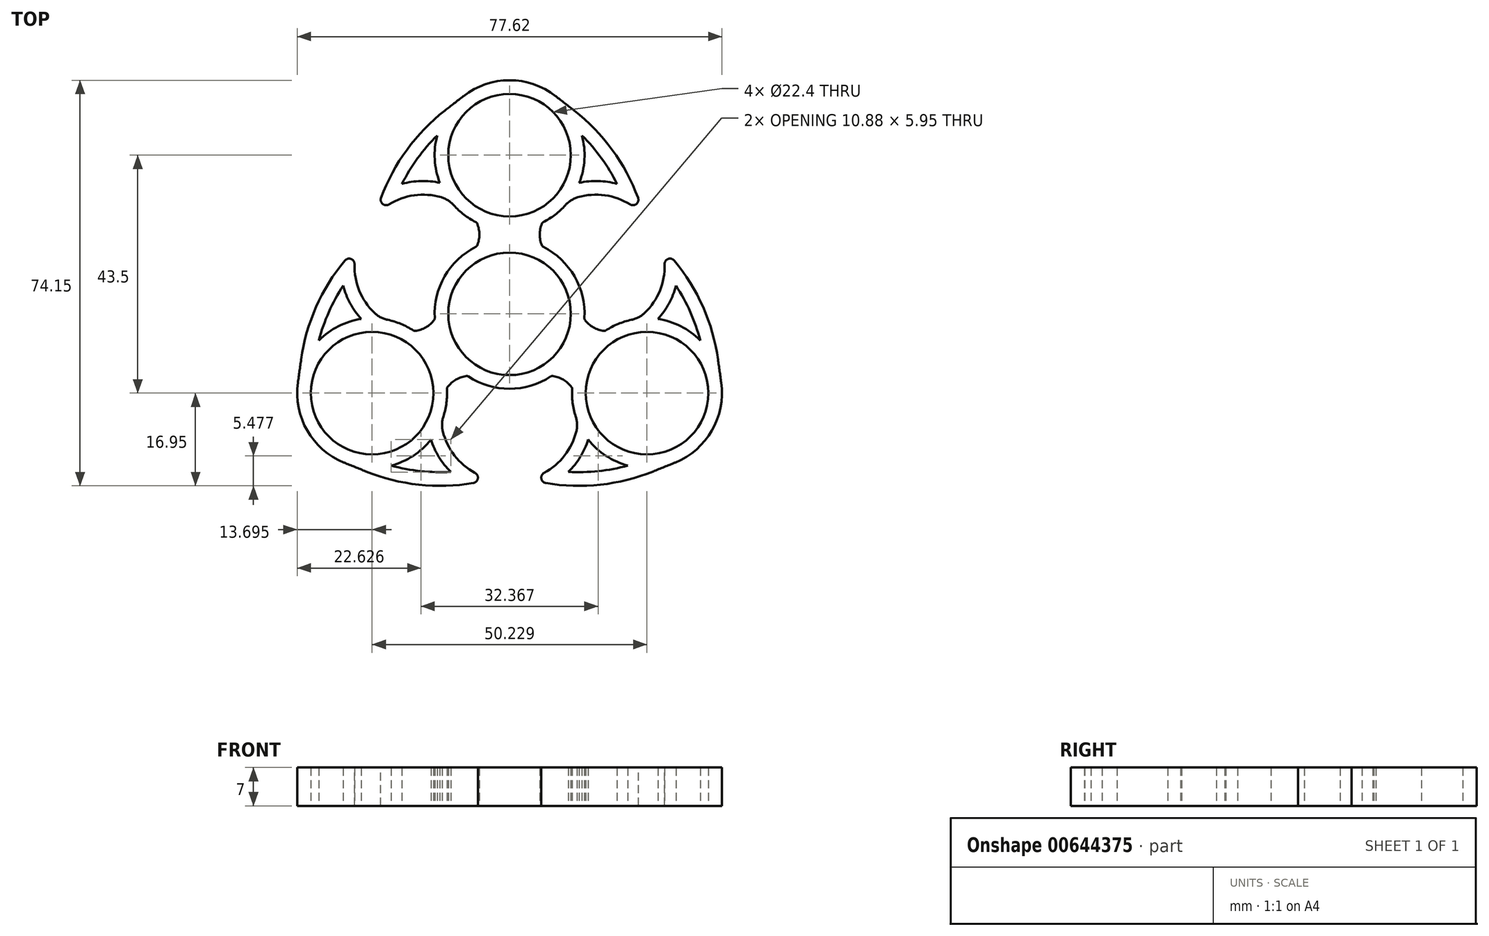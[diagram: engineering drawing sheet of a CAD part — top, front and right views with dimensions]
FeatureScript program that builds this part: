
annotation { "Feature Type Name" : "Feature", "Feature Type Description" : "" }
export const myFeature = defineFeature(function(context is Context, id is Id, definition is map)
    precondition{}
    {
        {
            var Q0;
            Q0=qCreatedBy(makeId("Top.planeOp"),FACE);
            var sketch = newSketch(context, id + "F0", { "sketchPlane" : qUnion([Q0])});
            skCircle(sketch, "E0", {"center": v(0, 0) * mm, "radius": 11.2 * mm});
            skLineSegment(sketch, "E1", {"start": v(0, 0) * mm, "end": v(0, 29) * mm, "construction": true});
            skCircle(sketch, "E2", {"center": v(0, 29) * mm, "radius": 11.2 * mm});
            skLineSegment(sketch, "E3", {"start": v(-11.2, 0) * mm, "end": v(11.2, 0) * mm, "construction": true});
            skLineSegment(sketch, "E4", {"start": v(-11.2, 29) * mm, "end": v(11.2, 29) * mm, "construction": true});
            skArc(sketch, "E5.0", {"start": v(-6, 12.32) * mm, "mid": v(0, -13.7) * mm, "end": v(6, 12.32) * mm});
            skLineSegment(sketch, "E6", {"start": v(0, 42.7) * mm, "end": v(0, 15.3) * mm, "construction": true});
            skLineSegment(sketch, "E7.0", {"start": v(6, 9.46) * mm, "end": v(6, 19.54) * mm, "construction": true});
            skArc(sketch, "E8", {"start": v(6, 16.68) * mm, "mid": v(5.52, 14.5) * mm, "end": v(6, 12.32) * mm});
            skArc(sketch, "E9.MirrorCS", {"start": v(-6, 16.68) * mm, "mid": v(-5.52, 14.5) * mm, "end": v(-6, 12.32) * mm});
            skArc(sketch, "E10.trimOffspring", {"start": v(6, 16.68) * mm, "mid": v(8.7, 18.4) * mm, "end": v(10.9, 20.71) * mm});
            skArc(sketch, "E11", {"start": v(24.52, 17.91) * mm, "mid": v(19, 29.66) * mm, "end": v(9.67, 38.7) * mm});
            skArc(sketch, "E12", {"start": v(24.52, 17.91) * mm, "mid": v(18.17, 21.54) * mm, "end": v(10.9, 20.71) * mm});
            skArc(sketch, "E13.0", {"start": v(19.65, 23.75) * mm, "mid": v(16.2, 24.27) * mm, "end": v(12.73, 23.95) * mm});
            skArc(sketch, "E13.1", {"start": v(19.65, 23.75) * mm, "mid": v(16.8, 28.44) * mm, "end": v(13.22, 32.6) * mm});
            skArc(sketch, "E14.trimOffspring", {"start": v(9.67, 38.7) * mm, "mid": v(-11.16, 36.94) * mm, "end": v(-6, 16.68) * mm});
            skArc(sketch, "E15.trimOffspring", {"start": v(12.73, 23.95) * mm, "mid": v(13.68, 28.23) * mm, "end": v(13.22, 32.6) * mm});
            skSolve(sketch);
        }
        {
            var Q0;
            Q0 = qSketchRegion(id + "F0", true);
            extrude(context, id + "F1", {"entities" : qUnion([Q0]), "depth" : 7 * mm, "offsetDistance" : 25 * mm});
        }
        {
            var Q0;
            Q0=qCreatedBy(makeId("Right.planeOp"),FACE);
            var sketch = newSketch(context, id + "F2", { "sketchPlane" : qUnion([Q0])});
            skLineSegment(sketch, "E16", {"start": v(0, 0) * mm, "end": v(0, 24.15) * mm, "construction": true});
            skSolve(sketch);
        }
        {
            var Q0;
            Q0=makeQuery(id+"F1.opExtrude","SWEPT_EDGE",EDGE,{"disambiguationData":[OSD([sQuery(id+"F0.wireOp",EDGE,"E11"),sQuery(id+"F0.wireOp",EDGE,"E12")])]});
            fillet(context, id + "F3", {"entities" : qUnion([Q0]), "radius" : 1 * mm, "tangentPropagation" : true, "allowEdgeOverflow" : false});
        }
        {
            var Q0;
            Q0=makeQuery(id+"F1.opExtrude","SWEPT_EDGE",EDGE,{"disambiguationData":[OSD([sQuery(id+"F0.wireOp",EDGE,"E10.trimOffspring"),sQuery(id+"F0.wireOp",EDGE,"E12")])]});
            fillet(context, id + "F4", {"entities" : qUnion([Q0]), "radius" : 5 * mm, "tangentPropagation" : true, "allowEdgeOverflow" : false});
        }
        {
            var Q0;
            Q0=makeQuery(id+"F1.opExtrude","SWEPT_EDGE",EDGE,{"disambiguationData":[OSD([sQuery(id+"F0.wireOp",EDGE,"E8"),sQuery(id+"F0.wireOp",EDGE,"a7715e3d-49e1-4b64-8228-6264ce36ffdd.trimOffspring")])]});
            var Q1;
            Q1=makeQuery(id+"F1.opExtrude","SWEPT_EDGE",EDGE,{"disambiguationData":[OSD([sQuery(id+"F0.wireOp",EDGE,"vL0yK9kr-aUAw-fq5m-LhdP-4na97wzfjfiJ"),sQuery(id+"F0.wireOp",EDGE,"a7715e3d-49e1-4b64-8228-6264ce36ffdd.trimOffspring")])]});
            var Q2;
            Q2=makeQuery(id+"F1.opExtrude","SWEPT_EDGE",EDGE,{"disambiguationData":[OSD([sQuery(id+"F0.wireOp",EDGE,"0uLAjghk-3gFu-Hscj-w9fE-ttjJYeJmuMDI"),sQuery(id+"F0.wireOp",EDGE,"vL0yK9kr-aUAw-fq5m-LhdP-4na97wzfjfiJ")])]});
            var Q3;
            Q3=makeQuery(id+"F1.opExtrude","SWEPT_EDGE",EDGE,{"disambiguationData":[OSD([sQuery(id+"F0.wireOp",EDGE,"59cc2289-ca77-47a6-96da-44b8b7f5bab30.MirrorCS"),sQuery(id+"F0.wireOp",EDGE,"5cff57ee-30ec-4a3f-ae05-e4d68d5af566.0")])]});
            var Q4;
            Q4=makeQuery(id+"F1.opExtrude","SWEPT_EDGE",EDGE,{"disambiguationData":[OSD([sQuery(id+"F0.wireOp",EDGE,"Nf5N08YX-LUpC-YIFK-iieG-ll9huf0In2a7"),sQuery(id+"F0.wireOp",EDGE,"59cc2289-ca77-47a6-96da-44b8b7f5bab30.MirrorCS")])]});
            var Q5;
            Q5=makeQuery(id+"F1.opExtrude","SWEPT_EDGE",EDGE,{"disambiguationData":[OSD([sQuery(id+"F0.wireOp",EDGE,"Nf5N08YX-LUpC-YIFK-iieG-ll9huf0In2a7"),sQuery(id+"F0.wireOp",EDGE,"8e5a45cd-34c5-40eb-b1f5-600c90d6d9e0.0")])]});
            var Q6;
            Q6=makeQuery(id+"F1.opExtrude","SWEPT_EDGE",EDGE,{"disambiguationData":[OSD([sQuery(id+"F0.wireOp",EDGE,"8e5a45cd-34c5-40eb-b1f5-600c90d6d9e0.0"),sQuery(id+"F0.wireOp",EDGE,"5cff57ee-30ec-4a3f-ae05-e4d68d5af566.0")])]});
            var Q7;
            Q7=makeQuery(id+"F1.opExtrude","SWEPT_EDGE",EDGE,{"disambiguationData":[OSD([sQuery(id+"F0.wireOp",EDGE,"E9.MirrorCS"),sQuery(id+"F0.wireOp",EDGE,"E14.trimOffspring")])]});
            var Q8;
            Q8=makeQuery(id+"F1.opExtrude","SWEPT_EDGE",EDGE,{"disambiguationData":[OSD([sQuery(id+"F0.wireOp",EDGE,"E5.0"),sQuery(id+"F0.wireOp",EDGE,"E9.MirrorCS")])]});
            fillet(context, id + "F5", {"entities" : qUnion([Q0, Q1, Q2, Q3, Q4, Q5, Q6, Q7, Q8]), "radius" : 0.5 * mm, "tangentPropagation" : true, "allowEdgeOverflow" : false});
        }
        {
            var Q0;
            Q0=makeQuery(id+"F1.opExtrude","SWEPT_EDGE",EDGE,{"disambiguationData":[OSD([sQuery(id+"F0.wireOp",EDGE,"E11"),sQuery(id+"F0.wireOp",EDGE,"E14.trimOffspring")])]});
            fillet(context, id + "F6", {"entities" : qUnion([Q0]), "radius" : 1952.43 * mm, "tangentPropagation" : true, "allowEdgeOverflow" : false});
        }
        {
            var Q0;
            Q0=makeQuery(id+"F1.opExtrude","SWEPT_BODY",BODY,{"disambiguationData":[OSD([sQuery(id+"F0.wireOp",EDGE,"E0"),sQuery(id+"F0.wireOp",EDGE,"E2"),sQuery(id+"F0.wireOp",EDGE,"E5.0"),sQuery(id+"F0.wireOp",EDGE,"beef2716-db7f-41ab-9648-4623db96a248.0"),sQuery(id+"F0.wireOp",EDGE,"0uLAjghk-3gFu-Hscj-w9fE-ttjJYeJmuMDI"),sQuery(id+"F0.wireOp",EDGE,"vL0yK9kr-aUAw-fq5m-LhdP-4na97wzfjfiJ"),sQuery(id+"F0.wireOp",EDGE,"c7e23209-4e23-4cac-a964-1c74d8cbfa74.0"),sQuery(id+"F0.wireOp",EDGE,"c7e23209-4e23-4cac-a964-1c74d8cbfa74.1"),sQuery(id+"F0.wireOp",EDGE,"df6599d3-b23b-4a78-9647-52215b223935.trimOffspring"),sQuery(id+"F0.wireOp",EDGE,"E8"),sQuery(id+"F0.wireOp",EDGE,"E9.MirrorCS"),sQuery(id+"F0.wireOp",EDGE,"7884432a-9f31-4921-b3fb-1dd42b4fd2c3.0"),sQuery(id+"F0.wireOp",EDGE,"36360b40-f322-41f0-b5ba-529e4c97dfdc.0"),sQuery(id+"F0.wireOp",EDGE,"c7395060-edcf-4106-a591-bdadd866a779.0"),sQuery(id+"F0.wireOp",EDGE,"68ec89d5-ddd9-4a57-ad5e-668f128be303.0"),sQuery(id+"F0.wireOp",EDGE,"a7715e3d-49e1-4b64-8228-6264ce36ffdd.trimOffspring")])]});
            var Q1;
            Q1=sQuery(id+"F2.wireOp",EDGE,"E16");
            circularPattern(context, id + "F7", {"operationType" : NewBodyOperationType.ADD, "entities" : qUnion([Q0]), "axis" : qUnion([Q1]), "angle" : 360 * degree, "instanceCount" : 3, "equalSpace" : true});
        }
        {
            var Q0;
            Q0=makeQuery(id+"F1.opExtrude","SWEPT_BODY",BODY,{"disambiguationData":[OSD([sQuery(id+"F0.wireOp",EDGE,"E0"),sQuery(id+"F0.wireOp",EDGE,"E2"),sQuery(id+"F0.wireOp",EDGE,"E5.0"),sQuery(id+"F0.wireOp",EDGE,"E8"),sQuery(id+"F0.wireOp",EDGE,"E9.MirrorCS"),sQuery(id+"F0.wireOp",EDGE,"Nf5N08YX-LUpC-YIFK-iieG-ll9huf0In2a7"),sQuery(id+"F0.wireOp",EDGE,"8e5a45cd-34c5-40eb-b1f5-600c90d6d9e0.0"),sQuery(id+"F0.wireOp",EDGE,"59cc2289-ca77-47a6-96da-44b8b7f5bab30.MirrorCS"),sQuery(id+"F0.wireOp",EDGE,"5cff57ee-30ec-4a3f-ae05-e4d68d5af566.0"),sQuery(id+"F0.wireOp",EDGE,"E10.trimOffspring"),sQuery(id+"F0.wireOp",EDGE,"E11"),sQuery(id+"F0.wireOp",EDGE,"E12"),sQuery(id+"F0.wireOp",EDGE,"E13.0"),sQuery(id+"F0.wireOp",EDGE,"E13.1"),sQuery(id+"F0.wireOp",EDGE,"E14.trimOffspring"),sQuery(id+"F0.wireOp",EDGE,"E15.trimOffspring")])]});
            var Q1;
            Q1=qCreatedBy(makeId("Right.planeOp"),FACE);
            mirror(context, id + "F8", {"operationType" : NewBodyOperationType.ADD, "entities" : qUnion([Q0]), "mirrorPlane" : qUnion([Q1])});
        }
    });
